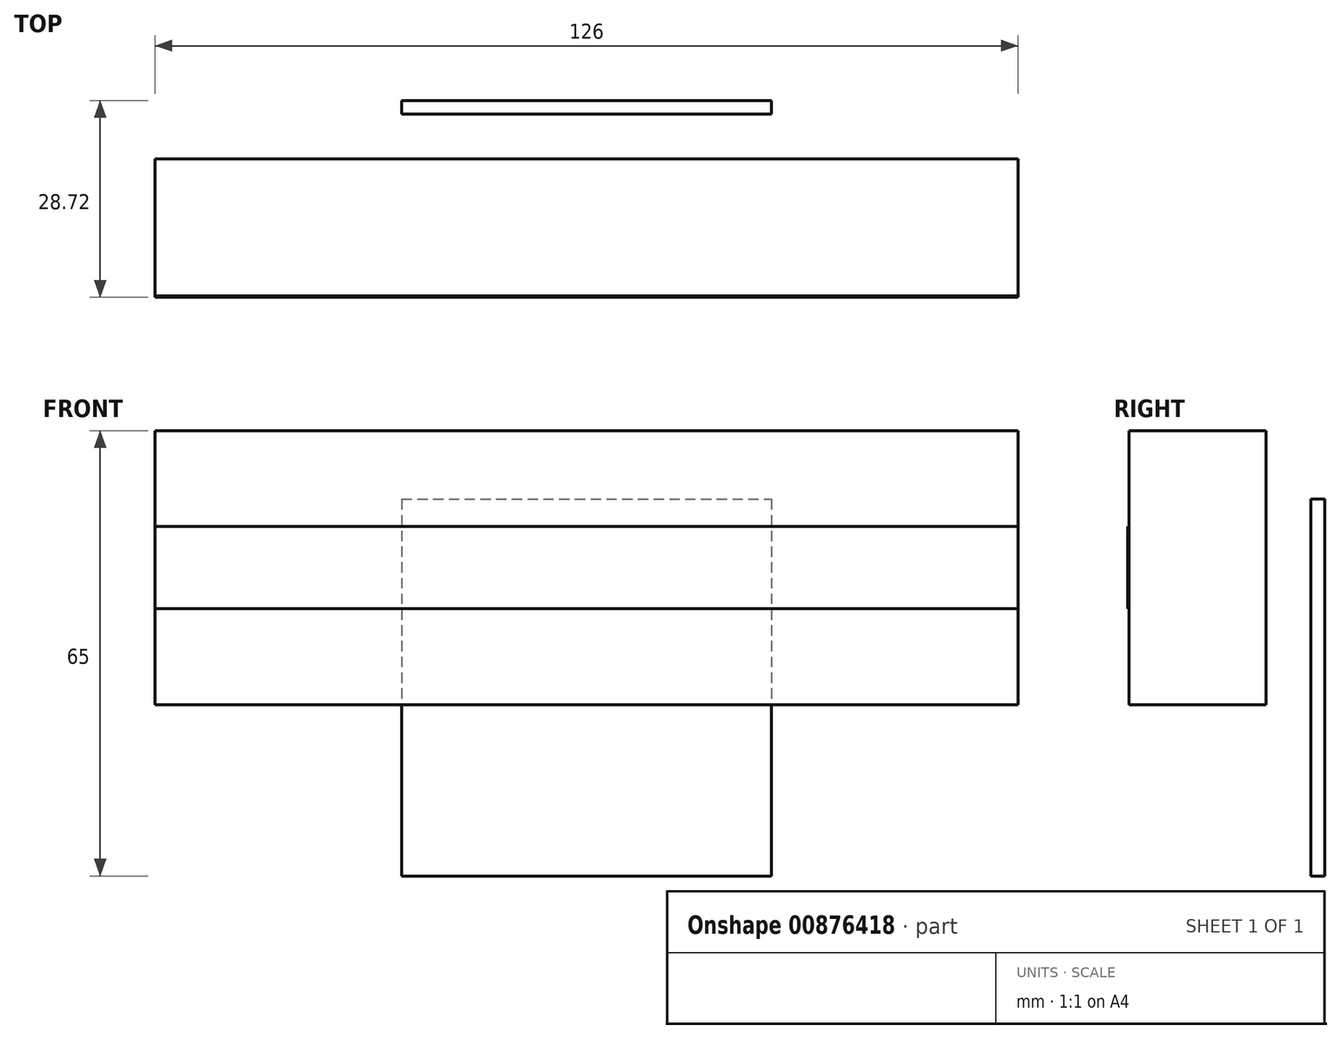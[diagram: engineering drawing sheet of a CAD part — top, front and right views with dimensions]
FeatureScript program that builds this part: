
annotation { "Feature Type Name" : "Feature", "Feature Type Description" : "" }
export const myFeature = defineFeature(function(context is Context, id is Id, definition is map)
    precondition{}
    {
        {
            var Q0;
            Q0=qCreatedBy(makeId("Front.planeOp"),FACE);
            var sketch = newSketch(context, id + "F0", { "sketchPlane" : qUnion([Q0])});
            skLineSegment(sketch, "E0.bottom", {"start": v(-27, 10) * mm, "end": v(27, 10) * mm});
            skLineSegment(sketch, "E0.top", {"start": v(-27, -45) * mm, "end": v(27, -45) * mm});
            skLineSegment(sketch, "E0.left", {"start": v(-27, 10) * mm, "end": v(-27, -45) * mm});
            skLineSegment(sketch, "E0.right", {"start": v(27, 10) * mm, "end": v(27, -45) * mm});
            skSolve(sketch);
        }
        {
            var Q0;
            Q0=makeQuery(id+"F0.imprint","IMPRINT",FACE,{"disambiguationData":[TD([[makeQuery(id+"F0.imprint","IMPRINT",EDGE,{"derivedFrom":sQuery(id+"F0.wireOp",EDGE,"E0.bottom")}),-1.0]])]});
            extrude(context, id + "F1", {"entities" : qUnion([Q0]), "oppositeDirection" : true, "depth" : 2.02 * mm, "offsetDistance" : 25 * mm});
        }
        {
            var Q0;
            Q0=qCreatedBy(makeId("Front.planeOp"),FACE);
            cPlane(context, id + "F2", {"entities" : qUnion([Q0]), "cplaneType" : CPlaneType.OFFSET, "offset" : 26.5 * mm, "width" : 150 * mm, "height" : 150 * mm});
        }
        {
            var Q0;
            Q0=qCreatedBy(id+"F2.planeOp",FACE);
            var sketch = newSketch(context, id + "F3", { "sketchPlane" : qUnion([Q0])});
            skLineSegment(sketch, "E1.bottom", {"start": v(-63, 20) * mm, "end": v(63, 20) * mm});
            skLineSegment(sketch, "E1.top", {"start": v(-63, -20) * mm, "end": v(63, -20) * mm});
            skLineSegment(sketch, "E1.left", {"start": v(-63, 20) * mm, "end": v(-63, -20) * mm});
            skLineSegment(sketch, "E1.right", {"start": v(63, 20) * mm, "end": v(63, -20) * mm});
            skLineSegment(sketch, "E2.bottom", {"start": v(-63, 6) * mm, "end": v(63, 6) * mm});
            skLineSegment(sketch, "E2.top", {"start": v(-63, -6) * mm, "end": v(63, -6) * mm});
            skLineSegment(sketch, "E2.left", {"start": v(-63, 6) * mm, "end": v(-63, -6) * mm});
            skLineSegment(sketch, "E2.right", {"start": v(63, 6) * mm, "end": v(63, -6) * mm});
            skSolve(sketch);
        }
        {
            var Q0;
            Q0=makeQuery(id+"F3.imprint","IMPRINT",FACE,{"disambiguationData":[TD([[makeQuery(id+"F3.imprint","IMPRINT",EDGE,{"derivedFrom":sQuery(id+"F3.wireOp",EDGE,"E1.bottom")}),-1.0]])]});
            var Q1;
            Q1=makeQuery(id+"F3.imprint","IMPRINT",FACE,{"disambiguationData":[TD([[makeQuery(id+"F3.imprint","IMPRINT",EDGE,{"derivedFrom":sQuery(id+"F3.wireOp",EDGE,"E2.bottom")}),-1.0]])]});
            var Q2;
            {var subQ0=sQuery(id+"F3.wireOp",EDGE,"E1.top");Q2=makeQuery(id+"F3.imprint","IMPRINT",FACE,{"disambiguationData":[TD([[makeQuery(id+"F3.imprint","IMPRINT",EDGE,{"derivedFrom":subQ0}),1.0]])]});}
            extrude(context, id + "F4", {"entities" : qUnion([Q0, Q1, Q2]), "oppositeDirection" : true, "depth" : 20 * mm, "offsetDistance" : 25 * mm});
        }
        {
            var Q0;
            Q0=makeQuery(id+"F3.imprint","IMPRINT",FACE,{"disambiguationData":[TD([[makeQuery(id+"F3.imprint","IMPRINT",EDGE,{"derivedFrom":sQuery(id+"F3.wireOp",EDGE,"E2.bottom")}),-1.0]])]});
            extrude(context, id + "F5", {"entities" : qUnion([Q0]), "depth" : 0.2 * mm, "offsetDistance" : 25 * mm});
        }
    });
